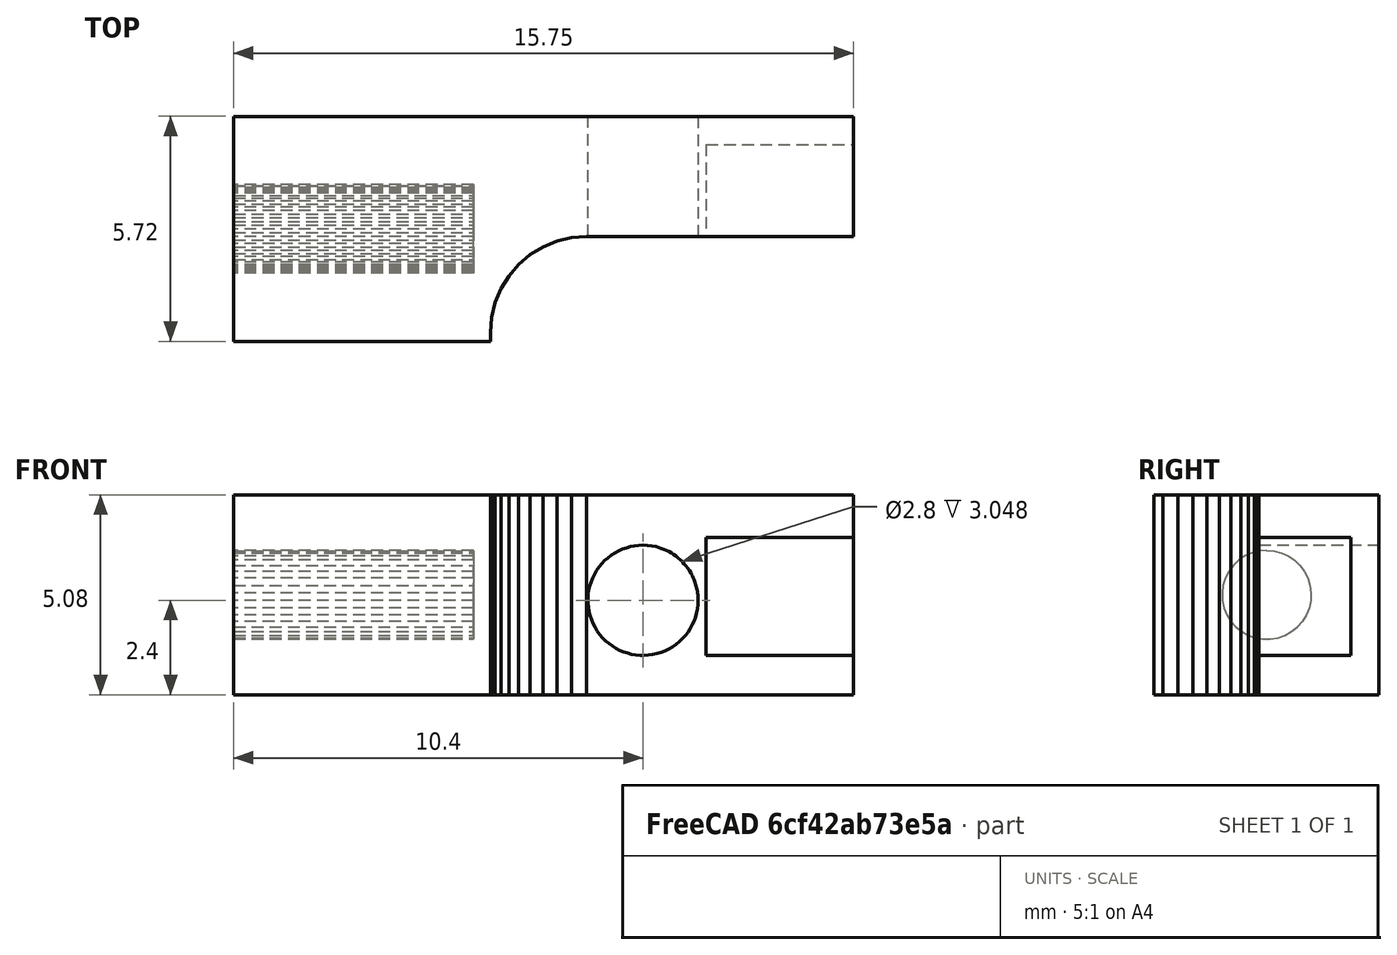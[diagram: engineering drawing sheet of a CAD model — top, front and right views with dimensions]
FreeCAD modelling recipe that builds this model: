
FCSTD DOCUMENT  (FreeCAD 0.21R33771 (Git))
Label: holder
License: All rights reserved
LicenseURL: https://en.wikipedia.org/wiki/All_rights_reserved
objects: Part::Feature×1, PartDesign::FeatureBase×1, PartDesign::SubtractiveBox×1, PartDesign::SubtractiveCylinder×1, PartDesign::Body×1
note: 7 computed .brp shape members not serialized (recipe doc carries the construction recipe); baked Part::Feature solids carry a one-line shape summary decoded from their .brp

FEATURE [Part::Feature] holder_Body002_solid  label="holder_Body002 (Solid)"
  shape: bbox 15.75 x 5.715 x 5.08 mm, 250 faces (baked)
FEATURE [PartDesign::FeatureBase] BaseFeature
  BaseFeature = -> holder_Body002_solid
FEATURE [PartDesign::SubtractiveBox] Box
  AttacherType = Attacher::AttachEngine3D
  AttachmentOffset = pos=(12,1,-5) rot=(0,0,1;0rad)
  BaseFeature = -> BaseFeature
  Height = 3
  Length = 4
  MapMode = 5
  Placement = pos=(12,5,1) rot=(1,0,0;1.5708rad)
  Support = -> [BaseFeature]
  Width = 3
FEATURE [PartDesign::SubtractiveCylinder] Cylinder
  Angle = 360
  AttacherType = Attacher::AttachEngine3D
  AttachmentOffset = pos=(-1.6,1.4,-9) rot=(0,0,1;0rad)
  BaseFeature = -> Box
  FirstAngle = 0
  Height = 10
  MapMode = 5
  Placement = pos=(10.4,9,2.4) rot=(1,0,0;1.5708rad)
  Radius = 1.4
  SecondAngle = 0
  Support = -> [Box]
FEATURE [PartDesign::Body] Body
  BaseFeature = -> holder_Body002_solid
  Group = -> [BaseFeature,Box,Cylinder]
  Origin = -> Origin
  Tip = -> Cylinder
